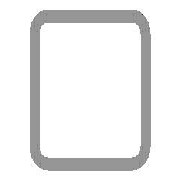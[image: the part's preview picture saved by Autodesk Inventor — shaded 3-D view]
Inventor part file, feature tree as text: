
AUTODESK INVENTOR PART (.ipt)
format: ipt  version: 2025.1 (Build 291241020, 241B)  size: 132,608 bytes
history: native  units: mm (DEFAULTED — no unit token found)
features: other x4, sketch x1, plane x1
ambient origin geometry x8: Origin, YZ Plane, XZ Plane, XY Plane, X Axis, Y Axis, Z Axis, Center Point
bodies: Solid1 (feature_tree), Body (feature_tree)
feature tree (6):
  parser-record x1  (decoder bookkeeping rows leaked as tree rows — omitted from the tree; the rows remain in map.json)
  other  "Driven Length"
  other  "Start Plane"
  other  "End Plane"
  sketch  "Sketch3"  dims[d3=290.0mm d4=0.0mm d7=4.0mm d9=40.0mm d11=40.0mm d12=2.0mm d13=40.0mm d14=330.0mm d15=20.0mm d16=20.0mm d17=90.0deg d18=290.0mm]
  plane  "Work Plane3"
